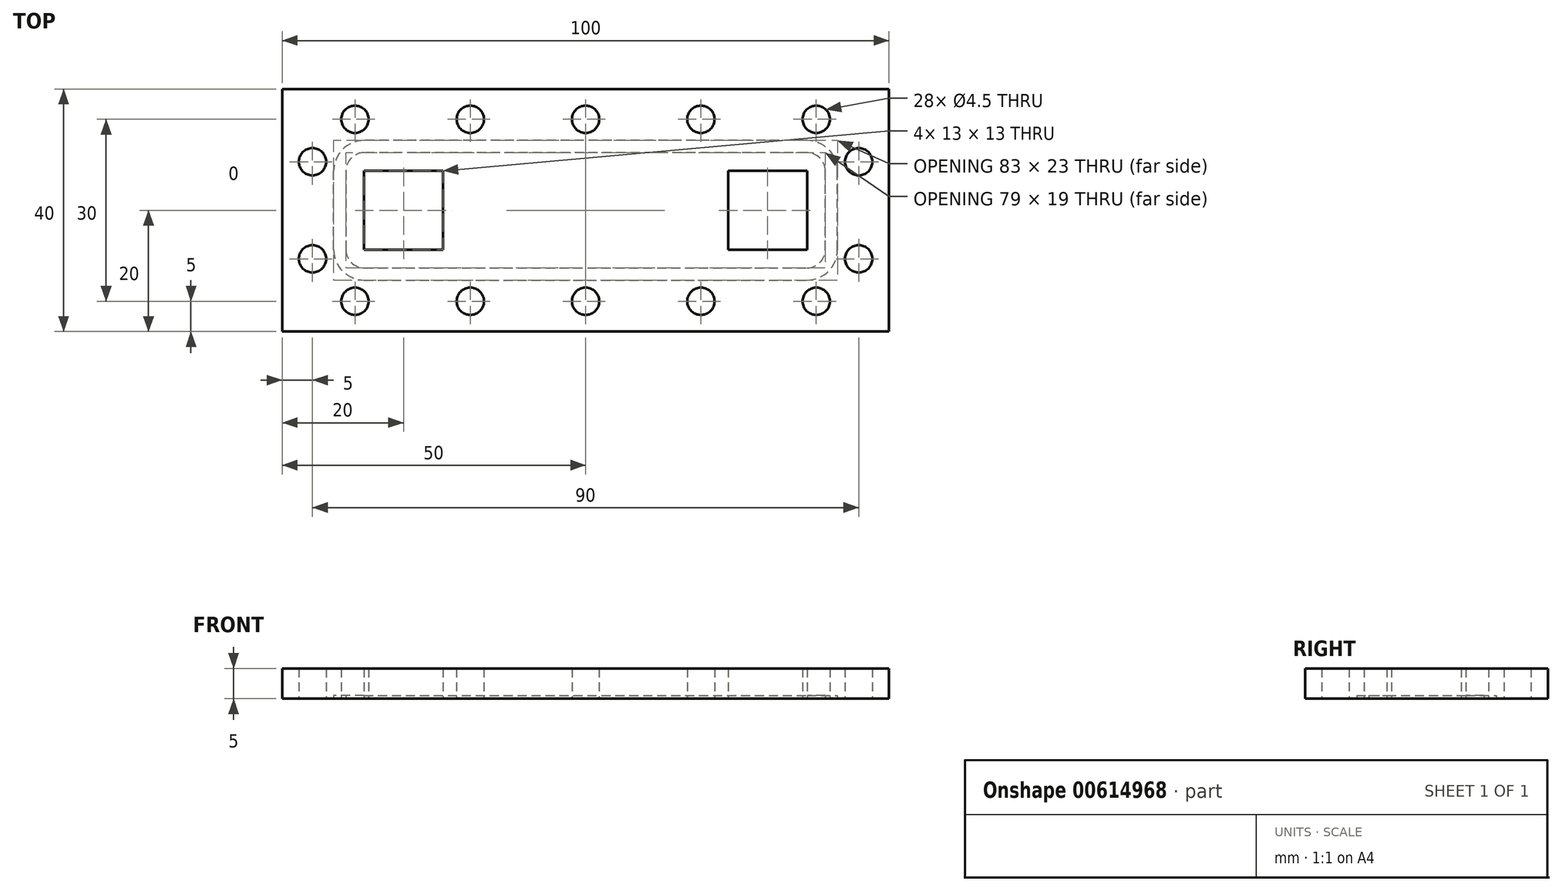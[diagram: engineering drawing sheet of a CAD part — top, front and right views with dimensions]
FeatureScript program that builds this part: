
annotation { "Feature Type Name" : "Feature", "Feature Type Description" : "" }
export const myFeature = defineFeature(function(context is Context, id is Id, definition is map)
    precondition{}
    {
        {
            var Q0;
            Q0=qCreatedBy(makeId("Top.planeOp"),FACE);
            var sketch = newSketch(context, id + "F0", { "sketchPlane" : qUnion([Q0])});
            skLineSegment(sketch, "E0.bottom", {"start": v(0, 0) * mm, "end": v(100, 0) * mm});
            skLineSegment(sketch, "E0.top", {"start": v(0, -40) * mm, "end": v(100, -40) * mm});
            skLineSegment(sketch, "E0.left", {"start": v(0, 0) * mm, "end": v(0, -40) * mm});
            skLineSegment(sketch, "E0.right", {"start": v(100, 0) * mm, "end": v(100, -40) * mm});
            skSolve(sketch);
        }
        {
            var Q0;
            Q0=makeQuery(id+"F0.imprint","IMPRINT",FACE,{"disambiguationData":[TD([[makeQuery(id+"F0.imprint","IMPRINT",EDGE,{"derivedFrom":sQuery(id+"F0.wireOp",EDGE,"E0.bottom")}),-1.0]])]});
            extrude(context, id + "F1", {"entities" : qUnion([Q0]), "depth" : 5 * mm, "offsetDistance" : 25 * mm});
        }
        {
            var Q0;
            Q0=qCreatedBy(makeId("Top.planeOp"),FACE);
            var sketch = newSketch(context, id + "F2", { "sketchPlane" : qUnion([Q0])});
            skCircle(sketch, "E1", {"center": v(5, -12) * mm, "radius": 2.25 * mm});
            skCircle(sketch, "E2", {"center": v(5, -28) * mm, "radius": 2.25 * mm});
            skCircle(sketch, "E3", {"center": v(12, -5) * mm, "radius": 2.25 * mm});
            skCircle(sketch, "E4", {"center": v(12, -35) * mm, "radius": 2.25 * mm});
            skCircle(sketch, "E5", {"center": v(31, -35) * mm, "radius": 2.25 * mm});
            skCircle(sketch, "E6", {"center": v(50, -35) * mm, "radius": 2.25 * mm});
            skCircle(sketch, "E7", {"center": v(69, -35) * mm, "radius": 2.25 * mm});
            skCircle(sketch, "E8", {"center": v(88, -35) * mm, "radius": 2.25 * mm});
            skCircle(sketch, "E9", {"center": v(95, -28) * mm, "radius": 2.25 * mm});
            skCircle(sketch, "E10", {"center": v(95, -12) * mm, "radius": 2.25 * mm});
            skCircle(sketch, "E11", {"center": v(88, -5) * mm, "radius": 2.25 * mm});
            skCircle(sketch, "E12", {"center": v(69, -5) * mm, "radius": 2.25 * mm});
            skCircle(sketch, "E13", {"center": v(50, -5) * mm, "radius": 2.25 * mm});
            skCircle(sketch, "E14", {"center": v(31, -5) * mm, "radius": 2.25 * mm});
            skSolve(sketch);
        }
        {
            var Q0;
            Q0=makeQuery(id+"F2.imprint","IMPRINT",FACE,{"disambiguationData":[TD([[makeQuery(id+"F2.imprint","IMPRINT",EDGE,{"derivedFrom":sQuery(id+"F2.wireOp",EDGE,"E4")}),1.0]])]});
            var Q1;
            Q1=makeQuery(id+"F2.imprint","IMPRINT",FACE,{"disambiguationData":[TD([[makeQuery(id+"F2.imprint","IMPRINT",EDGE,{"derivedFrom":sQuery(id+"F2.wireOp",EDGE,"E5")}),1.0]])]});
            var Q2;
            Q2=makeQuery(id+"F2.imprint","IMPRINT",FACE,{"disambiguationData":[TD([[makeQuery(id+"F2.imprint","IMPRINT",EDGE,{"derivedFrom":sQuery(id+"F2.wireOp",EDGE,"E6")}),1.0]])]});
            var Q3;
            Q3=makeQuery(id+"F2.imprint","IMPRINT",FACE,{"disambiguationData":[TD([[makeQuery(id+"F2.imprint","IMPRINT",EDGE,{"derivedFrom":sQuery(id+"F2.wireOp",EDGE,"E7")}),1.0]])]});
            var Q4;
            Q4=makeQuery(id+"F2.imprint","IMPRINT",FACE,{"disambiguationData":[TD([[makeQuery(id+"F2.imprint","IMPRINT",EDGE,{"derivedFrom":sQuery(id+"F2.wireOp",EDGE,"E8")}),1.0]])]});
            var Q5;
            Q5=makeQuery(id+"F2.imprint","IMPRINT",FACE,{"disambiguationData":[TD([[makeQuery(id+"F2.imprint","IMPRINT",EDGE,{"derivedFrom":sQuery(id+"F2.wireOp",EDGE,"E9")}),1.0]])]});
            var Q6;
            Q6=makeQuery(id+"F2.imprint","IMPRINT",FACE,{"disambiguationData":[TD([[makeQuery(id+"F2.imprint","IMPRINT",EDGE,{"derivedFrom":sQuery(id+"F2.wireOp",EDGE,"E10")}),1.0]])]});
            var Q7;
            Q7=makeQuery(id+"F2.imprint","IMPRINT",FACE,{"disambiguationData":[TD([[makeQuery(id+"F2.imprint","IMPRINT",EDGE,{"derivedFrom":sQuery(id+"F2.wireOp",EDGE,"E11")}),1.0]])]});
            var Q8;
            Q8=makeQuery(id+"F2.imprint","IMPRINT",FACE,{"disambiguationData":[TD([[makeQuery(id+"F2.imprint","IMPRINT",EDGE,{"derivedFrom":sQuery(id+"F2.wireOp",EDGE,"E12")}),1.0]])]});
            var Q9;
            Q9=makeQuery(id+"F2.imprint","IMPRINT",FACE,{"disambiguationData":[TD([[makeQuery(id+"F2.imprint","IMPRINT",EDGE,{"derivedFrom":sQuery(id+"F2.wireOp",EDGE,"E13")}),1.0]])]});
            var Q10;
            Q10=makeQuery(id+"F2.imprint","IMPRINT",FACE,{"disambiguationData":[TD([[makeQuery(id+"F2.imprint","IMPRINT",EDGE,{"derivedFrom":sQuery(id+"F2.wireOp",EDGE,"E14")}),1.0]])]});
            var Q11;
            Q11=makeQuery(id+"F2.imprint","IMPRINT",FACE,{"disambiguationData":[TD([[makeQuery(id+"F2.imprint","IMPRINT",EDGE,{"derivedFrom":sQuery(id+"F2.wireOp",EDGE,"E3")}),1.0]])]});
            var Q12;
            Q12=makeQuery(id+"F2.imprint","IMPRINT",FACE,{"disambiguationData":[TD([[makeQuery(id+"F2.imprint","IMPRINT",EDGE,{"derivedFrom":sQuery(id+"F2.wireOp",EDGE,"E1")}),1.0]])]});
            var Q13;
            Q13=makeQuery(id+"F2.imprint","IMPRINT",FACE,{"disambiguationData":[TD([[makeQuery(id+"F2.imprint","IMPRINT",EDGE,{"derivedFrom":sQuery(id+"F2.wireOp",EDGE,"E2")}),1.0]])]});
            extrude(context, id + "F3", {"entities" : qUnion([Q0, Q1, Q2, Q3, Q4, Q5, Q6, Q7, Q8, Q9, Q10, Q11, Q12, Q13]), "operationType" : NewBodyOperationType.REMOVE, "depth" : 18.9 * mm});
        }
        {
            var Q0;
            Q0=makeQuery(id+"F1.opExtrude","CAP_FACE",FACE,{"disambiguationData":[OSD([sQuery(id+"F0.wireOp",EDGE,"E0.bottom"),sQuery(id+"F0.wireOp",EDGE,"E0.top"),sQuery(id+"F0.wireOp",EDGE,"E0.left"),sQuery(id+"F0.wireOp",EDGE,"E0.right")])],"isStart":true});
            var sketch = newSketch(context, id + "F4", { "sketchPlane" : qUnion([Q0])});
            skLineSegment(sketch, "E15", {"start": v(100, 28.5) * mm, "end": v(91.5, 28.5) * mm});
            skLineSegment(sketch, "E16", {"start": v(91.5, 28.5) * mm, "end": v(91.5, 31.5) * mm});
            skLineSegment(sketch, "E17", {"start": v(91.5, 26.5) * mm, "end": v(91.5, 13.5) * mm});
            skLineSegment(sketch, "E18", {"start": v(91.5, 31.5) * mm, "end": v(89.5, 31.5) * mm});
            skLineSegment(sketch, "E19", {"start": v(89.5, 31.5) * mm, "end": v(89.5, 29.5) * mm});
            skLineSegment(sketch, "E20", {"start": v(89.5, 26.5) * mm, "end": v(89.5, 13.5) * mm});
            skLineSegment(sketch, "E21", {"start": v(86.5, 10.5) * mm, "end": v(13.5, 10.5) * mm});
            skLineSegment(sketch, "E22", {"start": v(10.5, 13.5) * mm, "end": v(10.5, 26.5) * mm});
            skLineSegment(sketch, "E23", {"start": v(13.5, 29.5) * mm, "end": v(86.5, 29.5) * mm});
            skPoint(sketch, "E24.visualSharp", {"position": v(89.5, 29.5) * mm});
            skArc(sketch, "E24.filletArc", {"start": v(89.5, 26.5) * mm, "mid": v(88.62, 28.62) * mm, "end": v(86.5, 29.5) * mm});
            skPoint(sketch, "E25.visualSharp", {"position": v(89.5, 10.5) * mm});
            skArc(sketch, "E25.filletArc", {"start": v(86.5, 10.5) * mm, "mid": v(88.62, 11.38) * mm, "end": v(89.5, 13.5) * mm});
            skPoint(sketch, "E26.visualSharp", {"position": v(10.5, 29.5) * mm});
            skArc(sketch, "E26.filletArc", {"start": v(13.5, 29.5) * mm, "mid": v(11.38, 28.62) * mm, "end": v(10.5, 26.5) * mm});
            skPoint(sketch, "E27.visualSharp", {"position": v(10.5, 10.5) * mm});
            skArc(sketch, "E27.filletArc", {"start": v(10.5, 13.5) * mm, "mid": v(11.38, 11.38) * mm, "end": v(13.5, 10.5) * mm});
            skPoint(sketch, "E28.visualSharp", {"position": v(91.5, 31.5) * mm});
            skArc(sketch, "E28.filletArc", {"start": v(91.5, 26.5) * mm, "mid": v(90.04, 30.04) * mm, "end": v(86.5, 31.5) * mm});
            skPoint(sketch, "E29.visualSharp", {"position": v(91.5, 8.5) * mm});
            skArc(sketch, "E29.filletArc", {"start": v(86.5, 8.5) * mm, "mid": v(90.04, 9.96) * mm, "end": v(91.5, 13.5) * mm});
            skPoint(sketch, "E30.visualSharp", {"position": v(6.5, 31.5) * mm});
            skLineSegment(sketch, "E31", {"start": v(13.5, 29.5) * mm, "end": v(13.5, 31.5) * mm});
            skLineSegment(sketch, "E32", {"start": v(13.5, 31.5) * mm, "end": v(13.5, 31.5) * mm});
            skLineSegment(sketch, "E33", {"start": v(8.5, 26.5) * mm, "end": v(8.5, 26.5) * mm});
            skLineSegment(sketch, "E34", {"start": v(8.5, 26.5) * mm, "end": v(8.5, 13.5) * mm});
            skLineSegment(sketch, "E35", {"start": v(8.5, 13.5) * mm, "end": v(8.5, 13.5) * mm});
            skLineSegment(sketch, "E36", {"start": v(13.5, 8.5) * mm, "end": v(13.5, 8.5) * mm});
            skPoint(sketch, "E37.visualSharp", {"position": v(8.5, 31.5) * mm});
            skArc(sketch, "E37.filletArc", {"start": v(13.5, 31.5) * mm, "mid": v(9.96, 30.04) * mm, "end": v(8.5, 26.5) * mm});
            skPoint(sketch, "E38.visualSharp", {"position": v(8.5, 8.5) * mm});
            skArc(sketch, "E38.filletArc", {"start": v(8.5, 13.5) * mm, "mid": v(9.96, 9.96) * mm, "end": v(13.5, 8.5) * mm});
            skLineSegment(sketch, "E39", {"start": v(13.5, 31.5) * mm, "end": v(86.5, 31.5) * mm});
            skLineSegment(sketch, "E40", {"start": v(86.5, 8.5) * mm, "end": v(13.5, 8.5) * mm});
            skSolve(sketch);
        }
        {
            var Q0;
            {var subQ1=sQuery(id+"F4.wireOp",EDGE,"E17");Q0=makeQuery(id+"F4.imprint","IMPRINT",FACE,{"disambiguationData":[TD([[makeQuery(id+"F4.imprint","IMPRINT",EDGE,{"derivedFrom":subQ1}),-1.0]])]});}
            extrude(context, id + "F5", {"entities" : qUnion([Q0]), "operationType" : NewBodyOperationType.REMOVE, "oppositeDirection" : true, "depth" : 0.5 * mm, "offsetDistance" : 25 * mm});
        }
        {
            var Q0;
            {var subQ0=sQuery(id+"F0.wireOp",EDGE,"E0.left");var subQ1=sQuery(id+"F0.wireOp",EDGE,"E0.top");var subQ2=sQuery(id+"F0.wireOp",EDGE,"E0.right");var subQ3=sQuery(id+"F0.wireOp",EDGE,"E0.bottom");Q0=makeQuery(id+"F5.boolean.opBoolean","SPLIT",FACE,{"disambiguationData":[TD([makeQuery(id+"F1.opExtrude","SWEPT_FACE",FACE,{"disambiguationData":[OSD([subQ3])]})])],"derivedFrom":makeQuery(id+"F1.opExtrude","CAP_FACE",FACE,{"disambiguationData":[OSD([subQ3,subQ1,subQ0,subQ2])],"isStart":true})});}
            var sketch = newSketch(context, id + "F6", { "sketchPlane" : qUnion([Q0])});
            skLineSegment(sketch, "E41", {"start": v(0, 0) * mm, "end": v(15, 0) * mm});
            skLineSegment(sketch, "E42", {"start": v(100, 0) * mm, "end": v(100, 13.5) * mm});
            skLineSegment(sketch, "E43", {"start": v(100, 13.5) * mm, "end": v(85, 13.5) * mm});
            skLineSegment(sketch, "E44", {"start": v(16, 13.5) * mm, "end": v(0, 13.5) * mm});
            skLineSegment(sketch, "E45", {"start": v(85, 13.5) * mm, "end": v(84, 13.5) * mm});
            skLineSegment(sketch, "E46", {"start": v(100, 13.5) * mm, "end": v(86.5, 13.5) * mm});
            skLineSegment(sketch, "E47", {"start": v(86.5, 13.5) * mm, "end": v(86.5, 26.5) * mm});
            skLineSegment(sketch, "E48", {"start": v(86.5, 26.5) * mm, "end": v(73.5, 26.5) * mm});
            skLineSegment(sketch, "E49", {"start": v(73.5, 26.5) * mm, "end": v(73.5, 13.5) * mm});
            skLineSegment(sketch, "E50", {"start": v(73.5, 13.5) * mm, "end": v(86.5, 13.5) * mm});
            skLineSegment(sketch, "E51", {"start": v(0, 13.5) * mm, "end": v(13.5, 13.5) * mm});
            skLineSegment(sketch, "E52", {"start": v(13.5, 13.5) * mm, "end": v(13.5, 26.5) * mm});
            skLineSegment(sketch, "E53", {"start": v(13.5, 26.5) * mm, "end": v(26.5, 26.5) * mm});
            skLineSegment(sketch, "E54", {"start": v(26.5, 26.5) * mm, "end": v(26.5, 13.5) * mm});
            skLineSegment(sketch, "E55", {"start": v(26.5, 13.5) * mm, "end": v(13.5, 13.5) * mm});
            skLineSegment(sketch, "E56", {"start": v(73.5, 26.5) * mm, "end": v(26.5, 26.5) * mm});
            skLineSegment(sketch, "E57", {"start": v(86.5, 13.5) * mm, "end": v(13.5, 13.5) * mm});
            skSolve(sketch);
        }
        {
            var Q0;
            {var subQ3=sQuery(id+"F6.wireOp",EDGE,"E47");Q0=makeQuery(id+"F6.imprint","IMPRINT",FACE,{"disambiguationData":[TD([[makeQuery(id+"F6.imprint","IMPRINT",EDGE,{"derivedFrom":subQ3}),1.0]])]});}
            var Q1;
            {var subQ3=sQuery(id+"F6.wireOp",EDGE,"E52");Q1=makeQuery(id+"F6.imprint","IMPRINT",FACE,{"disambiguationData":[TD([[makeQuery(id+"F6.imprint","IMPRINT",EDGE,{"derivedFrom":subQ3}),-1.0]])]});}
            extrude(context, id + "F7", {"entities" : qUnion([Q0, Q1]), "operationType" : NewBodyOperationType.REMOVE, "oppositeDirection" : true, "depth" : 5 * mm, "offsetDistance" : 25 * mm});
        }
    });
